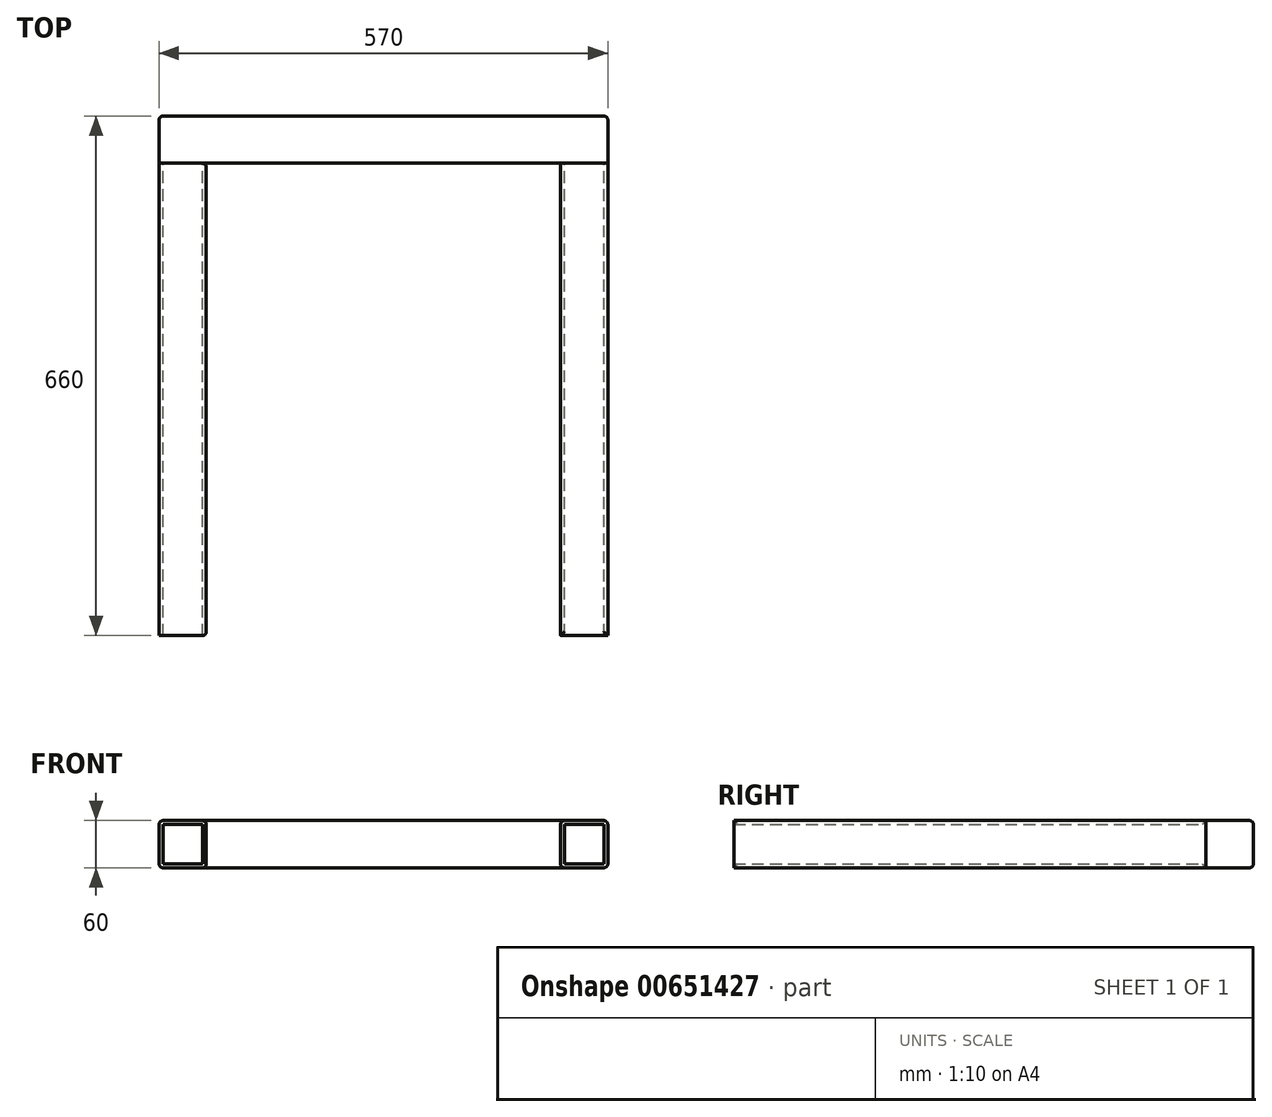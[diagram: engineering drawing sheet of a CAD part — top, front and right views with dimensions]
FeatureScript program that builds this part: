
annotation { "Feature Type Name" : "Feature", "Feature Type Description" : "" }
export const myFeature = defineFeature(function(context is Context, id is Id, definition is map)
    precondition{}
    {
        {
            var Q0;
            Q0=qCreatedBy(makeId("Front.planeOp"),FACE);
            var sketch = newSketch(context, id + "F0", { "sketchPlane" : qUnion([Q0])});
            skLineSegment(sketch, "E0.bottom", {"start": v(225, 60) * mm, "end": v(285, 60) * mm});
            skLineSegment(sketch, "E0.top", {"start": v(225, 0) * mm, "end": v(285, 0) * mm});
            skLineSegment(sketch, "E0.left", {"start": v(225, 60) * mm, "end": v(225, 0) * mm});
            skLineSegment(sketch, "E0.right", {"start": v(285, 60) * mm, "end": v(285, 0) * mm});
            skLineSegment(sketch, "E1.bottom", {"start": v(230, 55) * mm, "end": v(280, 55) * mm});
            skLineSegment(sketch, "E1.top", {"start": v(230, 5) * mm, "end": v(280, 5) * mm});
            skLineSegment(sketch, "E1.left", {"start": v(230, 55) * mm, "end": v(230, 5) * mm});
            skLineSegment(sketch, "E1.right", {"start": v(280, 55) * mm, "end": v(280, 5) * mm});
            skLineSegment(sketch, "E2.MirrorCS", {"start": v(-225, 60) * mm, "end": v(-225, 0) * mm});
            skLineSegment(sketch, "E3.MirrorCS", {"start": v(-230, 55) * mm, "end": v(-230, 5) * mm});
            skLineSegment(sketch, "E4.MirrorCS", {"start": v(-225, 60) * mm, "end": v(-285, 60) * mm});
            skLineSegment(sketch, "E5.MirrorCS", {"start": v(-230, 55) * mm, "end": v(-280, 55) * mm});
            skLineSegment(sketch, "E6.MirrorCS", {"start": v(-285, 60) * mm, "end": v(-285, 0) * mm});
            skLineSegment(sketch, "E7.MirrorCS", {"start": v(-280, 55) * mm, "end": v(-280, 5) * mm});
            skLineSegment(sketch, "E8.MirrorCS", {"start": v(-230, 5) * mm, "end": v(-280, 5) * mm});
            skLineSegment(sketch, "E9.MirrorCS", {"start": v(-225, 0) * mm, "end": v(-285, 0) * mm});
            skSolve(sketch);
        }
        {
            var Q0;
            Q0 = qSketchRegion(id + "F0", true);
            extrude(context, id + "F1", {"entities" : qUnion([Q0]), "depth" : 600 * mm, "offsetDistance" : 25 * mm});
        }
        {
            var Q0;
            Q0=qCreatedBy(makeId("Right.planeOp"),FACE);
            var sketch = newSketch(context, id + "F2", { "sketchPlane" : qUnion([Q0])});
            skLineSegment(sketch, "E10.bottom", {"start": v(0, 60) * mm, "end": v(60, 60) * mm});
            skLineSegment(sketch, "E10.top", {"start": v(0, 0) * mm, "end": v(60, 0) * mm});
            skLineSegment(sketch, "E10.left", {"start": v(0, 60) * mm, "end": v(0, 0) * mm});
            skLineSegment(sketch, "E10.right", {"start": v(60, 60) * mm, "end": v(60, 0) * mm});
            skSolve(sketch);
        }
        {
            var Q0;
            Q0 = qSketchRegion(id + "F2", true);
            extrude(context, id + "F3", {"entities" : qUnion([Q0]), "endBound" : BoundingType.SYMMETRIC, "depth" : 570 * mm, "offsetDistance" : 25 * mm});
        }
        {
            var Q0;
            Q0=makeQuery(id+"F3.opExtrude","SWEPT_FACE",FACE,{"disambiguationData":[OSD([sQuery(id+"F2.wireOp",EDGE,"E10.right")])]});
            var Q1;
            Q1=makeQuery(id+"F1.opExtrude","SWEPT_FACE",FACE,{"disambiguationData":[OSD([sQuery(id+"F0.wireOp",EDGE,"E2.MirrorCS")])]});
            var Q2;
            Q2=makeQuery(id+"F1.opExtrude","SWEPT_EDGE",EDGE,{"disambiguationData":[OSD([sQuery(id+"F0.wireOp",EDGE,"E0.bottom"),sQuery(id+"F0.wireOp",EDGE,"E0.left")])]});
            var Q3;
            Q3=makeQuery(id+"F1.opExtrude","CAP_EDGE",EDGE,{"disambiguationData":[OSD([sQuery(id+"F0.wireOp",EDGE,"E0.bottom")])],"isStart":false});
            var Q4;
            Q4=makeQuery(id+"F3.opExtrude","CAP_EDGE",EDGE,{"disambiguationData":[OSD([sQuery(id+"F2.wireOp",EDGE,"E10.bottom")])],"isStart":true});
            var Q5;
            Q5=makeQuery(id+"F3.opExtrude","CAP_EDGE",EDGE,{"disambiguationData":[OSD([sQuery(id+"F2.wireOp",EDGE,"E10.top")])],"isStart":true});
            var Q6;
            Q6=makeQuery(id+"F1.opExtrude","SWEPT_EDGE",EDGE,{"disambiguationData":[OSD([sQuery(id+"F0.wireOp",EDGE,"E4.MirrorCS"),sQuery(id+"F0.wireOp",EDGE,"E6.MirrorCS")])]});
            var Q7;
            Q7=makeQuery(id+"F1.opExtrude","SWEPT_EDGE",EDGE,{"disambiguationData":[OSD([sQuery(id+"F0.wireOp",EDGE,"E6.MirrorCS"),sQuery(id+"F0.wireOp",EDGE,"E9.MirrorCS")])]});
            var Q8;
            Q8=makeQuery(id+"F1.opExtrude","SWEPT_EDGE",EDGE,{"disambiguationData":[OSD([sQuery(id+"F0.wireOp",EDGE,"E0.bottom"),sQuery(id+"F0.wireOp",EDGE,"E0.right")])]});
            var Q9;
            Q9=makeQuery(id+"F3.opExtrude","CAP_EDGE",EDGE,{"disambiguationData":[OSD([sQuery(id+"F2.wireOp",EDGE,"E10.bottom")])],"isStart":false});
            var Q10;
            Q10=makeQuery(id+"F3.opExtrude","CAP_EDGE",EDGE,{"disambiguationData":[OSD([sQuery(id+"F2.wireOp",EDGE,"E10.top")])],"isStart":false});
            var Q11;
            Q11=makeQuery(id+"F1.opExtrude","SWEPT_EDGE",EDGE,{"disambiguationData":[OSD([sQuery(id+"F0.wireOp",EDGE,"E0.top"),sQuery(id+"F0.wireOp",EDGE,"E0.right")])]});
            var Q12;
            Q12=makeQuery(id+"F1.opExtrude","SWEPT_EDGE",EDGE,{"disambiguationData":[OSD([sQuery(id+"F0.wireOp",EDGE,"E0.top"),sQuery(id+"F0.wireOp",EDGE,"E0.left")])]});
            fillet(context, id + "F4", {"entities" : qUnion([Q0, Q1, Q2, Q3, Q4, Q5, Q6, Q7, Q8, Q9, Q10, Q11, Q12]), "radius" : 5 * mm, "tangentPropagation" : true, "allowEdgeOverflow" : false});
        }
    });
